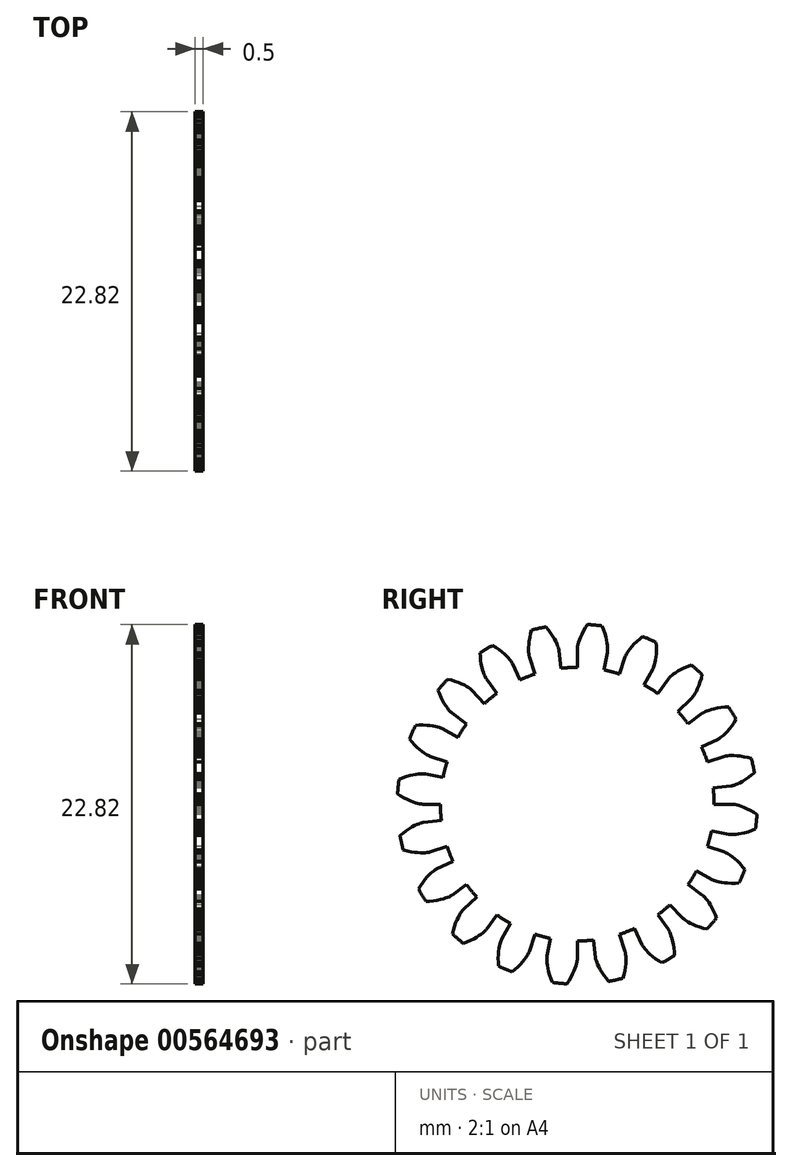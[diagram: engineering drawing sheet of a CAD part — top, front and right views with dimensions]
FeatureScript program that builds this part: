
annotation { "Feature Type Name" : "Feature", "Feature Type Description" : "" }
export const myFeature = defineFeature(function(context is Context, id is Id, definition is map)
    precondition{}
    {
        {
            assignVariable(context, id + "F0", {"name" : "GearThickness", "anyValue" : .5});
        }
        {
            var Q0;
            Q0=qCreatedBy(makeId("Right.planeOp"),FACE);
            var sketch = newSketch(context, id + "F1", { "sketchPlane" : qUnion([Q0])});
            skCircle(sketch, "E0", {"center": v(0, 0) * mm, "radius": 8.7 * mm});
            skCircle(sketch, "E1", {"center": v(0, 0) * mm, "radius": 9.84 * mm, "construction": true});
            skCircle(sketch, "E2", {"center": v(0, 0) * mm, "radius": 10.16 * mm, "construction": true});
            skCircle(sketch, "E3", {"center": v(0, 0) * mm, "radius": 11.43 * mm});
            skLineSegment(sketch, "E4", {"start": v(0, 0) * mm, "end": v(-9.84, 0) * mm, "construction": true});
            skLineSegment(sketch, "E5.1.0", {"start": v(0, 0) * mm, "end": v(-9.82, 0.5) * mm, "construction": true});
            skLineSegment(sketch, "E5.2.0", {"start": v(0, 0) * mm, "end": v(-9.79, 0.98) * mm, "construction": true});
            skLineSegment(sketch, "E5.3.0", {"start": v(0, 0) * mm, "end": v(-9.73, 1.47) * mm, "construction": true});
            skLineSegment(sketch, "E5.4.0", {"start": v(0, 0) * mm, "end": v(-9.64, 1.95) * mm, "construction": true});
            skLineSegment(sketch, "E5.5.0", {"start": v(0, 0) * mm, "end": v(-9.53, 2.43) * mm, "construction": true});
            skLineSegment(sketch, "E5.6.0", {"start": v(0, 0) * mm, "end": v(-9.4, 2.9) * mm, "construction": true});
            skLineSegment(sketch, "E5.7.0", {"start": v(0, 0) * mm, "end": v(-9.24, 3.37) * mm, "construction": true});
            skLineSegment(sketch, "E5.8.0", {"start": v(0, 0) * mm, "end": v(-9.06, 3.83) * mm, "construction": true});
            skLineSegment(sketch, "E5.9.0", {"start": v(0, 0) * mm, "end": v(-8.86, 4.28) * mm, "construction": true});
            skLineSegment(sketch, "E5.10.0", {"start": v(0, 0) * mm, "end": v(-8.63, 4.72) * mm, "construction": true});
            skLineSegment(sketch, "E5.11.0", {"start": v(0, 0) * mm, "end": v(-8.39, 5.14) * mm, "construction": true});
            skLineSegment(sketch, "E5.12.0", {"start": v(0, 0) * mm, "end": v(-8.12, 5.55) * mm, "construction": true});
            skLineSegment(sketch, "E5.13.0", {"start": v(0, 0) * mm, "end": v(-7.83, 5.95) * mm, "construction": true});
            skLineSegment(sketch, "E5.14.0", {"start": v(0, 0) * mm, "end": v(-7.52, 6.34) * mm, "construction": true});
            skLineSegment(sketch, "E5.anchor2", {"start": v(0, 0) * mm, "end": v(-7.52, 6.34) * mm, "construction": true});
            skLineSegment(sketch, "E6", {"start": v(-9.82, 0.5) * mm, "end": v(-9.85, 0) * mm, "construction": true});
            skLineSegment(sketch, "E7", {"start": v(-9.79, 0.98) * mm, "end": v(-9.89, 0) * mm, "construction": true});
            skLineSegment(sketch, "E8", {"start": v(-9.73, 1.47) * mm, "end": v(-9.95, 0.01) * mm, "construction": true});
            skLineSegment(sketch, "E9", {"start": v(-9.53, 2.43) * mm, "end": v(-10.14, 0.05) * mm, "construction": true});
            skLineSegment(sketch, "E10", {"start": v(-9.4, 2.9) * mm, "end": v(-10.27, 0.09) * mm, "construction": true});
            skLineSegment(sketch, "E11", {"start": v(-9.24, 3.37) * mm, "end": v(-10.42, 0.14) * mm, "construction": true});
            skLineSegment(sketch, "E12", {"start": v(-9.06, 3.83) * mm, "end": v(-10.6, 0.2) * mm, "construction": true});
            skLineSegment(sketch, "E13", {"start": v(-8.86, 4.28) * mm, "end": v(-10.78, 0.3) * mm, "construction": true});
            skLineSegment(sketch, "E14", {"start": v(-8.63, 4.72) * mm, "end": v(-11, 0.4) * mm, "construction": true});
            skLineSegment(sketch, "E15", {"start": v(-8.39, 5.14) * mm, "end": v(-11.21, 0.53) * mm, "construction": true});
            skLineSegment(sketch, "E16", {"start": v(-9.64, 1.95) * mm, "end": v(-10.03, 0.03) * mm, "construction": true});
            skLineSegment(sketch, "E17", {"start": v(-8.12, 5.55) * mm, "end": v(-11.45, 0.68) * mm, "construction": true});
            skLineSegment(sketch, "E18", {"start": v(-7.83, 5.95) * mm, "end": v(-11.7, 0.86) * mm, "construction": true});
            skLineSegment(sketch, "E19", {"start": v(-7.52, 6.34) * mm, "end": v(-11.96, 1.07) * mm, "construction": true});
            skLineSegment(sketch, "E20", {"start": v(0, 0) * mm, "end": v(-9.79, 0.96) * mm, "construction": true});
            skLineSegment(sketch, "E21", {"start": v(-8.7, 0) * mm, "end": v(-9.84, 0) * mm});
            skLineSegment(sketch, "E22.MirrorCS", {"start": v(-8.52, 1.7) * mm, "end": v(-9.65, 1.92) * mm});
            skLineSegment(sketch, "E23", {"start": v(-9.84, 0) * mm, "end": v(-9.85, 0) * mm});
            skLineSegment(sketch, "E24", {"start": v(-9.85, 0) * mm, "end": v(-9.89, 0) * mm});
            skLineSegment(sketch, "E25", {"start": v(-9.89, 0) * mm, "end": v(-9.95, 0.01) * mm});
            skLineSegment(sketch, "E26", {"start": v(-9.95, 0.01) * mm, "end": v(-10.03, 0.03) * mm});
            skLineSegment(sketch, "E27", {"start": v(-10.03, 0.03) * mm, "end": v(-10.14, 0.05) * mm});
            skLineSegment(sketch, "E28", {"start": v(-10.14, 0.05) * mm, "end": v(-10.27, 0.09) * mm});
            skLineSegment(sketch, "E29", {"start": v(-10.27, 0.09) * mm, "end": v(-10.42, 0.14) * mm});
            skLineSegment(sketch, "E30", {"start": v(-10.42, 0.14) * mm, "end": v(-10.6, 0.2) * mm});
            skLineSegment(sketch, "E31", {"start": v(-10.6, 0.2) * mm, "end": v(-10.78, 0.3) * mm});
            skLineSegment(sketch, "E32", {"start": v(-10.78, 0.3) * mm, "end": v(-11, 0.4) * mm});
            skLineSegment(sketch, "E33", {"start": v(-11, 0.4) * mm, "end": v(-11.21, 0.53) * mm});
            skLineSegment(sketch, "E34", {"start": v(-11.21, 0.53) * mm, "end": v(-11.45, 0.68) * mm});
            skLineSegment(sketch, "E35", {"start": v(-11.45, 0.68) * mm, "end": v(-11.7, 0.86) * mm});
            skLineSegment(sketch, "E36", {"start": v(-11.7, 0.86) * mm, "end": v(-11.96, 1.07) * mm});
            skLineSegment(sketch, "E37.MirrorCS", {"start": v(-9.65, 1.92) * mm, "end": v(-9.66, 1.92) * mm});
            skLineSegment(sketch, "E38.MirrorCS", {"start": v(-9.66, 1.92) * mm, "end": v(-9.7, 1.93) * mm});
            skLineSegment(sketch, "E39.MirrorCS", {"start": v(-9.7, 1.93) * mm, "end": v(-9.76, 1.93) * mm});
            skLineSegment(sketch, "E40.MirrorCS", {"start": v(-9.76, 1.93) * mm, "end": v(-9.84, 1.93) * mm});
            skLineSegment(sketch, "E41.MirrorCS", {"start": v(-9.95, 1.93) * mm, "end": v(-10.09, 1.92) * mm});
            skLineSegment(sketch, "E42.MirrorCS", {"start": v(-10.09, 1.92) * mm, "end": v(-10.25, 1.9) * mm});
            skLineSegment(sketch, "E43.MirrorCS", {"start": v(-10.25, 1.9) * mm, "end": v(-10.43, 1.86) * mm});
            skLineSegment(sketch, "E44.MirrorCS", {"start": v(-10.43, 1.86) * mm, "end": v(-10.63, 1.82) * mm});
            skLineSegment(sketch, "E45.MirrorCS", {"start": v(-10.86, 1.75) * mm, "end": v(-11.1, 1.67) * mm});
            skLineSegment(sketch, "E46.MirrorCS", {"start": v(-10.63, 1.82) * mm, "end": v(-10.86, 1.75) * mm});
            skLineSegment(sketch, "E47.MirrorCS", {"start": v(-11.1, 1.67) * mm, "end": v(-11.36, 1.56) * mm});
            skLineSegment(sketch, "E48.MirrorCS", {"start": v(-11.36, 1.56) * mm, "end": v(-11.64, 1.44) * mm});
            skLineSegment(sketch, "E49.MirrorCS", {"start": v(-11.64, 1.44) * mm, "end": v(-11.94, 1.28) * mm});
            skLineSegment(sketch, "E50.MirrorCS", {"start": v(-9.84, 1.93) * mm, "end": v(-9.95, 1.93) * mm});
            skLineSegment(sketch, "E51.1.0", {"start": v(-8.27, -2.69) * mm, "end": v(-9.35, -3.04) * mm});
            skLineSegment(sketch, "E51.1.1", {"start": v(-11.07, -1.84) * mm, "end": v(-11.3, -2.02) * mm});
            skLineSegment(sketch, "E51.1.2", {"start": v(-8.63, -1.02) * mm, "end": v(-9.77, -1.16) * mm});
            skLineSegment(sketch, "E51.1.3", {"start": v(-10.87, -1.69) * mm, "end": v(-11.07, -1.84) * mm});
            skLineSegment(sketch, "E51.1.4", {"start": v(-10.58, -3.02) * mm, "end": v(-10.83, -2.96) * mm});
            skLineSegment(sketch, "E51.1.5", {"start": v(-10.83, -2.96) * mm, "end": v(-11.1, -2.89) * mm});
            skLineSegment(sketch, "E51.1.6", {"start": v(-10.67, -1.56) * mm, "end": v(-10.87, -1.69) * mm});
            skLineSegment(sketch, "E51.1.7", {"start": v(-11.52, -2.23) * mm, "end": v(-11.75, -2.47) * mm});
            skLineSegment(sketch, "E51.1.8", {"start": v(-10.5, -1.45) * mm, "end": v(-10.67, -1.56) * mm});
            skLineSegment(sketch, "E51.1.9", {"start": v(-11.4, -2.8) * mm, "end": v(-11.7, -2.68) * mm});
            skLineSegment(sketch, "E51.1.10", {"start": v(-11.3, -2.02) * mm, "end": v(-11.52, -2.23) * mm});
            skLineSegment(sketch, "E51.1.11", {"start": v(-10.35, -3.05) * mm, "end": v(-10.58, -3.02) * mm});
            skLineSegment(sketch, "E51.1.12", {"start": v(-11.1, -2.89) * mm, "end": v(-11.4, -2.8) * mm});
            skLineSegment(sketch, "E51.1.13", {"start": v(-10.06, -1.24) * mm, "end": v(-10.19, -1.3) * mm});
            skLineSegment(sketch, "E51.1.14", {"start": v(-10.19, -1.3) * mm, "end": v(-10.33, -1.36) * mm});
            skLineSegment(sketch, "E51.1.15", {"start": v(-10.33, -1.36) * mm, "end": v(-10.5, -1.45) * mm});
            skLineSegment(sketch, "E51.1.16", {"start": v(-9.95, -3.09) * mm, "end": v(-10.14, -3.08) * mm});
            skLineSegment(sketch, "E51.1.17", {"start": v(-9.8, -3.09) * mm, "end": v(-9.95, -3.09) * mm});
            skLineSegment(sketch, "E51.1.18", {"start": v(-10.14, -3.08) * mm, "end": v(-10.35, -3.05) * mm});
            skLineSegment(sketch, "E51.1.19", {"start": v(-9.96, -1.2) * mm, "end": v(-10.06, -1.24) * mm});
            skLineSegment(sketch, "E51.1.20", {"start": v(-9.88, -1.18) * mm, "end": v(-9.96, -1.2) * mm});
            skLineSegment(sketch, "E51.1.21", {"start": v(-9.66, -3.08) * mm, "end": v(-9.8, -3.09) * mm});
            skLineSegment(sketch, "E51.1.22", {"start": v(-9.55, -3.07) * mm, "end": v(-9.66, -3.08) * mm});
            skLineSegment(sketch, "E51.1.23", {"start": v(-9.4, -3.05) * mm, "end": v(-9.46, -3.06) * mm});
            skLineSegment(sketch, "E51.1.24", {"start": v(-9.77, -1.16) * mm, "end": v(-9.78, -1.16) * mm});
            skLineSegment(sketch, "E51.1.25", {"start": v(-9.78, -1.16) * mm, "end": v(-9.82, -1.17) * mm});
            skLineSegment(sketch, "E51.1.26", {"start": v(-9.46, -3.06) * mm, "end": v(-9.55, -3.07) * mm});
            skLineSegment(sketch, "E51.1.27", {"start": v(-9.82, -1.17) * mm, "end": v(-9.88, -1.18) * mm});
            skLineSegment(sketch, "E51.1.28", {"start": v(-9.37, -3.04) * mm, "end": v(-9.4, -3.05) * mm});
            skLineSegment(sketch, "E51.1.29", {"start": v(-9.35, -3.04) * mm, "end": v(-9.37, -3.04) * mm});
            skLineSegment(sketch, "E51.2.0", {"start": v(-7.03, -5.1) * mm, "end": v(-7.96, -5.78) * mm});
            skLineSegment(sketch, "E51.2.1", {"start": v(-9.96, -5.18) * mm, "end": v(-10.11, -5.41) * mm});
            skLineSegment(sketch, "E51.2.2", {"start": v(-7.9, -3.64) * mm, "end": v(-8.93, -4.12) * mm});
            skLineSegment(sketch, "E51.2.3", {"start": v(-9.81, -4.96) * mm, "end": v(-9.96, -5.18) * mm});
            skLineSegment(sketch, "E51.2.4", {"start": v(-9.13, -6.14) * mm, "end": v(-9.38, -6.16) * mm});
            skLineSegment(sketch, "E51.2.5", {"start": v(-9.38, -6.16) * mm, "end": v(-9.67, -6.18) * mm});
            skLineSegment(sketch, "E51.2.6", {"start": v(-9.67, -4.78) * mm, "end": v(-9.81, -4.96) * mm});
            skLineSegment(sketch, "E51.2.7", {"start": v(-10.26, -5.68) * mm, "end": v(-10.41, -5.98) * mm});
            skLineSegment(sketch, "E51.2.8", {"start": v(-9.53, -4.62) * mm, "end": v(-9.67, -4.78) * mm});
            skLineSegment(sketch, "E51.2.9", {"start": v(-9.97, -6.18) * mm, "end": v(-10.3, -6.16) * mm});
            skLineSegment(sketch, "E51.2.10", {"start": v(-10.11, -5.41) * mm, "end": v(-10.26, -5.68) * mm});
            skLineSegment(sketch, "E51.2.11", {"start": v(-8.9, -6.1) * mm, "end": v(-9.13, -6.14) * mm});
            skLineSegment(sketch, "E51.2.12", {"start": v(-9.67, -6.18) * mm, "end": v(-9.97, -6.18) * mm});
            skLineSegment(sketch, "E51.2.13", {"start": v(-9.19, -4.3) * mm, "end": v(-9.29, -4.38) * mm});
            skLineSegment(sketch, "E51.2.14", {"start": v(-9.29, -4.38) * mm, "end": v(-9.4, -4.49) * mm});
            skLineSegment(sketch, "E51.2.15", {"start": v(-9.4, -4.49) * mm, "end": v(-9.53, -4.62) * mm});
            skLineSegment(sketch, "E51.2.16", {"start": v(-8.51, -6.01) * mm, "end": v(-8.7, -6.06) * mm});
            skLineSegment(sketch, "E51.2.17", {"start": v(-8.36, -5.97) * mm, "end": v(-8.51, -6.01) * mm});
            skLineSegment(sketch, "E51.2.18", {"start": v(-8.7, -6.06) * mm, "end": v(-8.9, -6.1) * mm});
            skLineSegment(sketch, "E51.2.19", {"start": v(-9.1, -4.22) * mm, "end": v(-9.19, -4.3) * mm});
            skLineSegment(sketch, "E51.2.20", {"start": v(-9.03, -4.17) * mm, "end": v(-9.1, -4.22) * mm});
            skLineSegment(sketch, "E51.2.21", {"start": v(-8.23, -5.92) * mm, "end": v(-8.36, -5.97) * mm});
            skLineSegment(sketch, "E51.2.22", {"start": v(-8.13, -5.88) * mm, "end": v(-8.23, -5.92) * mm});
            skLineSegment(sketch, "E51.2.23", {"start": v(-8, -5.8) * mm, "end": v(-8.05, -5.84) * mm});
            skLineSegment(sketch, "E51.2.24", {"start": v(-8.93, -4.12) * mm, "end": v(-8.94, -4.12) * mm});
            skLineSegment(sketch, "E51.2.25", {"start": v(-8.94, -4.12) * mm, "end": v(-8.98, -4.14) * mm});
            skLineSegment(sketch, "E51.2.26", {"start": v(-8.05, -5.84) * mm, "end": v(-8.13, -5.88) * mm});
            skLineSegment(sketch, "E51.2.27", {"start": v(-8.98, -4.14) * mm, "end": v(-9.03, -4.17) * mm});
            skLineSegment(sketch, "E51.2.28", {"start": v(-7.97, -5.79) * mm, "end": v(-8, -5.8) * mm});
            skLineSegment(sketch, "E51.2.29", {"start": v(-7.96, -5.78) * mm, "end": v(-7.97, -5.79) * mm});
            skLineSegment(sketch, "E51.3.0", {"start": v(-5.1, -7.03) * mm, "end": v(-5.78, -7.96) * mm});
            skLineSegment(sketch, "E51.3.1", {"start": v(-7.88, -8) * mm, "end": v(-7.94, -8.27) * mm});
            skLineSegment(sketch, "E51.3.2", {"start": v(-6.38, -5.9) * mm, "end": v(-7.22, -6.68) * mm});
            skLineSegment(sketch, "E51.3.3", {"start": v(-7.8, -7.75) * mm, "end": v(-7.88, -8) * mm});
            skLineSegment(sketch, "E51.3.4", {"start": v(-6.78, -8.66) * mm, "end": v(-7.02, -8.76) * mm});
            skLineSegment(sketch, "E51.3.5", {"start": v(-7.02, -8.76) * mm, "end": v(-7.28, -8.86) * mm});
            skLineSegment(sketch, "E51.3.6", {"start": v(-7.72, -7.53) * mm, "end": v(-7.8, -7.75) * mm});
            skLineSegment(sketch, "E51.3.7", {"start": v(-8, -8.58) * mm, "end": v(-8.06, -8.9) * mm});
            skLineSegment(sketch, "E51.3.8", {"start": v(-7.64, -7.34) * mm, "end": v(-7.72, -7.53) * mm});
            skLineSegment(sketch, "E51.3.9", {"start": v(-7.58, -8.96) * mm, "end": v(-7.9, -9.05) * mm});
            skLineSegment(sketch, "E51.3.10", {"start": v(-7.94, -8.27) * mm, "end": v(-8, -8.58) * mm});
            skLineSegment(sketch, "E51.3.11", {"start": v(-6.57, -8.55) * mm, "end": v(-6.78, -8.66) * mm});
            skLineSegment(sketch, "E51.3.12", {"start": v(-7.28, -8.86) * mm, "end": v(-7.58, -8.96) * mm});
            skLineSegment(sketch, "E51.3.13", {"start": v(-7.41, -6.92) * mm, "end": v(-7.48, -7.04) * mm});
            skLineSegment(sketch, "E51.3.14", {"start": v(-7.48, -7.04) * mm, "end": v(-7.56, -7.18) * mm});
            skLineSegment(sketch, "E51.3.15", {"start": v(-7.56, -7.18) * mm, "end": v(-7.64, -7.34) * mm});
            skLineSegment(sketch, "E51.3.16", {"start": v(-6.24, -8.35) * mm, "end": v(-6.4, -8.45) * mm});
            skLineSegment(sketch, "E51.3.17", {"start": v(-6.1, -8.26) * mm, "end": v(-6.24, -8.35) * mm});
            skLineSegment(sketch, "E51.3.18", {"start": v(-6.4, -8.45) * mm, "end": v(-6.57, -8.55) * mm});
            skLineSegment(sketch, "E51.3.19", {"start": v(-7.35, -6.83) * mm, "end": v(-7.41, -6.92) * mm});
            skLineSegment(sketch, "E51.3.20", {"start": v(-7.3, -6.76) * mm, "end": v(-7.35, -6.83) * mm});
            skLineSegment(sketch, "E51.3.21", {"start": v(-6, -8.17) * mm, "end": v(-6.1, -8.26) * mm});
            skLineSegment(sketch, "E51.3.22", {"start": v(-5.92, -8.1) * mm, "end": v(-6, -8.17) * mm});
            skLineSegment(sketch, "E51.3.23", {"start": v(-5.81, -8) * mm, "end": v(-5.86, -8.04) * mm});
            skLineSegment(sketch, "E51.3.24", {"start": v(-7.22, -6.68) * mm, "end": v(-7.23, -6.69) * mm});
            skLineSegment(sketch, "E51.3.25", {"start": v(-7.23, -6.69) * mm, "end": v(-7.26, -6.71) * mm});
            skLineSegment(sketch, "E51.3.26", {"start": v(-5.86, -8.04) * mm, "end": v(-5.92, -8.1) * mm});
            skLineSegment(sketch, "E51.3.27", {"start": v(-7.26, -6.71) * mm, "end": v(-7.3, -6.76) * mm});
            skLineSegment(sketch, "E51.3.28", {"start": v(-5.79, -7.97) * mm, "end": v(-5.81, -8) * mm});
            skLineSegment(sketch, "E51.3.29", {"start": v(-5.78, -7.96) * mm, "end": v(-5.79, -7.97) * mm});
            skLineSegment(sketch, "E51.4.0", {"start": v(-2.69, -8.27) * mm, "end": v(-3.04, -9.35) * mm});
            skLineSegment(sketch, "E51.4.1", {"start": v(-5.02, -10.04) * mm, "end": v(-5, -10.32) * mm});
            skLineSegment(sketch, "E51.4.2", {"start": v(-4.25, -7.58) * mm, "end": v(-4.8, -8.58) * mm});
            skLineSegment(sketch, "E51.4.3", {"start": v(-5.02, -9.78) * mm, "end": v(-5.02, -10.04) * mm});
            skLineSegment(sketch, "E51.4.4", {"start": v(-3.78, -10.33) * mm, "end": v(-3.97, -10.5) * mm});
            skLineSegment(sketch, "E51.4.5", {"start": v(-3.97, -10.5) * mm, "end": v(-4.19, -10.68) * mm});
            skLineSegment(sketch, "E51.4.6", {"start": v(-5.01, -9.55) * mm, "end": v(-5.02, -9.78) * mm});
            skLineSegment(sketch, "E51.4.7", {"start": v(-4.96, -10.63) * mm, "end": v(-4.9, -10.96) * mm});
            skLineSegment(sketch, "E51.4.8", {"start": v(-5, -9.34) * mm, "end": v(-5.01, -9.55) * mm});
            skLineSegment(sketch, "E51.4.9", {"start": v(-4.44, -10.86) * mm, "end": v(-4.71, -11.04) * mm});
            skLineSegment(sketch, "E51.4.10", {"start": v(-5, -10.32) * mm, "end": v(-4.96, -10.63) * mm});
            skLineSegment(sketch, "E51.4.11", {"start": v(-3.61, -10.16) * mm, "end": v(-3.78, -10.33) * mm});
            skLineSegment(sketch, "E51.4.12", {"start": v(-4.19, -10.68) * mm, "end": v(-4.44, -10.86) * mm});
            skLineSegment(sketch, "E51.4.13", {"start": v(-4.9, -8.87) * mm, "end": v(-4.94, -9) * mm});
            skLineSegment(sketch, "E51.4.14", {"start": v(-4.94, -9) * mm, "end": v(-4.97, -9.16) * mm});
            skLineSegment(sketch, "E51.4.15", {"start": v(-4.97, -9.16) * mm, "end": v(-5, -9.34) * mm});
            skLineSegment(sketch, "E51.4.16", {"start": v(-3.35, -9.87) * mm, "end": v(-3.47, -10) * mm});
            skLineSegment(sketch, "E51.4.17", {"start": v(-3.26, -9.74) * mm, "end": v(-3.35, -9.87) * mm});
            skLineSegment(sketch, "E51.4.18", {"start": v(-3.47, -10) * mm, "end": v(-3.61, -10.16) * mm});
            skLineSegment(sketch, "E51.4.19", {"start": v(-4.88, -8.76) * mm, "end": v(-4.9, -8.87) * mm});
            skLineSegment(sketch, "E51.4.20", {"start": v(-4.85, -8.68) * mm, "end": v(-4.88, -8.76) * mm});
            skLineSegment(sketch, "E51.4.21", {"start": v(-3.18, -9.63) * mm, "end": v(-3.26, -9.74) * mm});
            skLineSegment(sketch, "E51.4.22", {"start": v(-3.12, -9.53) * mm, "end": v(-3.18, -9.63) * mm});
            skLineSegment(sketch, "E51.4.23", {"start": v(-3.06, -9.4) * mm, "end": v(-3.08, -9.46) * mm});
            skLineSegment(sketch, "E51.4.24", {"start": v(-4.8, -8.58) * mm, "end": v(-4.81, -8.6) * mm});
            skLineSegment(sketch, "E51.4.25", {"start": v(-4.81, -8.6) * mm, "end": v(-4.83, -8.63) * mm});
            skLineSegment(sketch, "E51.4.26", {"start": v(-3.08, -9.46) * mm, "end": v(-3.12, -9.53) * mm});
            skLineSegment(sketch, "E51.4.27", {"start": v(-4.83, -8.63) * mm, "end": v(-4.85, -8.68) * mm});
            skLineSegment(sketch, "E51.4.28", {"start": v(-3.04, -9.37) * mm, "end": v(-3.06, -9.4) * mm});
            skLineSegment(sketch, "E51.4.29", {"start": v(-3.04, -9.35) * mm, "end": v(-3.04, -9.37) * mm});
            skLineSegment(sketch, "E51.5.0", {"start": v(0, -8.7) * mm, "end": v(0, -9.84) * mm});
            skLineSegment(sketch, "E51.5.1", {"start": v(-1.67, -11.1) * mm, "end": v(-1.56, -11.36) * mm});
            skLineSegment(sketch, "E51.5.2", {"start": v(-1.7, -8.52) * mm, "end": v(-1.92, -9.65) * mm});
            skLineSegment(sketch, "E51.5.3", {"start": v(-1.75, -10.86) * mm, "end": v(-1.67, -11.1) * mm});
            skLineSegment(sketch, "E51.5.4", {"start": v(-0.4, -11) * mm, "end": v(-0.53, -11.21) * mm});
            skLineSegment(sketch, "E51.5.5", {"start": v(-0.53, -11.21) * mm, "end": v(-0.68, -11.45) * mm});
            skLineSegment(sketch, "E51.5.6", {"start": v(-1.82, -10.63) * mm, "end": v(-1.75, -10.86) * mm});
            skLineSegment(sketch, "E51.5.7", {"start": v(-1.44, -11.64) * mm, "end": v(-1.28, -11.94) * mm});
            skLineSegment(sketch, "E51.5.8", {"start": v(-1.86, -10.43) * mm, "end": v(-1.82, -10.63) * mm});
            skLineSegment(sketch, "E51.5.9", {"start": v(-0.86, -11.7) * mm, "end": v(-1.07, -11.96) * mm});
            skLineSegment(sketch, "E51.5.10", {"start": v(-1.56, -11.36) * mm, "end": v(-1.44, -11.64) * mm});
            skLineSegment(sketch, "E51.5.11", {"start": v(-0.3, -10.78) * mm, "end": v(-0.4, -11) * mm});
            skLineSegment(sketch, "E51.5.12", {"start": v(-0.68, -11.45) * mm, "end": v(-0.86, -11.7) * mm});
            skLineSegment(sketch, "E51.5.13", {"start": v(-1.93, -9.95) * mm, "end": v(-1.92, -10.09) * mm});
            skLineSegment(sketch, "E51.5.14", {"start": v(-1.92, -10.09) * mm, "end": v(-1.9, -10.25) * mm});
            skLineSegment(sketch, "E51.5.15", {"start": v(-1.9, -10.25) * mm, "end": v(-1.86, -10.43) * mm});
            skLineSegment(sketch, "E51.5.16", {"start": v(-0.14, -10.42) * mm, "end": v(-0.2, -10.6) * mm});
            skLineSegment(sketch, "E51.5.17", {"start": v(-0.09, -10.27) * mm, "end": v(-0.14, -10.42) * mm});
            skLineSegment(sketch, "E51.5.18", {"start": v(-0.2, -10.6) * mm, "end": v(-0.3, -10.78) * mm});
            skLineSegment(sketch, "E51.5.19", {"start": v(-1.93, -9.84) * mm, "end": v(-1.93, -9.95) * mm});
            skLineSegment(sketch, "E51.5.20", {"start": v(-1.93, -9.76) * mm, "end": v(-1.93, -9.84) * mm});
            skLineSegment(sketch, "E51.5.21", {"start": v(-0.05, -10.14) * mm, "end": v(-0.09, -10.27) * mm});
            skLineSegment(sketch, "E51.5.22", {"start": v(-0.03, -10.03) * mm, "end": v(-0.05, -10.14) * mm});
            skLineSegment(sketch, "E51.5.23", {"start": v(0, -9.89) * mm, "end": v(-0.01, -9.95) * mm});
            skLineSegment(sketch, "E51.5.24", {"start": v(-1.92, -9.65) * mm, "end": v(-1.92, -9.66) * mm});
            skLineSegment(sketch, "E51.5.25", {"start": v(-1.92, -9.66) * mm, "end": v(-1.93, -9.7) * mm});
            skLineSegment(sketch, "E51.5.26", {"start": v(-0.01, -9.95) * mm, "end": v(-0.03, -10.03) * mm});
            skLineSegment(sketch, "E51.5.27", {"start": v(-1.93, -9.7) * mm, "end": v(-1.93, -9.76) * mm});
            skLineSegment(sketch, "E51.5.28", {"start": v(0, -9.85) * mm, "end": v(0, -9.89) * mm});
            skLineSegment(sketch, "E51.5.29", {"start": v(0, -9.84) * mm, "end": v(0, -9.85) * mm});
            skLineSegment(sketch, "E51.6.0", {"start": v(2.69, -8.27) * mm, "end": v(3.04, -9.35) * mm});
            skLineSegment(sketch, "E51.6.1", {"start": v(1.84, -11.07) * mm, "end": v(2.02, -11.3) * mm});
            skLineSegment(sketch, "E51.6.2", {"start": v(1.02, -8.63) * mm, "end": v(1.16, -9.77) * mm});
            skLineSegment(sketch, "E51.6.3", {"start": v(1.69, -10.87) * mm, "end": v(1.84, -11.07) * mm});
            skLineSegment(sketch, "E51.6.4", {"start": v(3.02, -10.58) * mm, "end": v(2.96, -10.83) * mm});
            skLineSegment(sketch, "E51.6.5", {"start": v(2.96, -10.83) * mm, "end": v(2.89, -11.1) * mm});
            skLineSegment(sketch, "E51.6.6", {"start": v(1.56, -10.67) * mm, "end": v(1.69, -10.87) * mm});
            skLineSegment(sketch, "E51.6.7", {"start": v(2.23, -11.52) * mm, "end": v(2.47, -11.75) * mm});
            skLineSegment(sketch, "E51.6.8", {"start": v(1.45, -10.5) * mm, "end": v(1.56, -10.67) * mm});
            skLineSegment(sketch, "E51.6.9", {"start": v(2.8, -11.4) * mm, "end": v(2.68, -11.7) * mm});
            skLineSegment(sketch, "E51.6.10", {"start": v(2.02, -11.3) * mm, "end": v(2.23, -11.52) * mm});
            skLineSegment(sketch, "E51.6.11", {"start": v(3.05, -10.35) * mm, "end": v(3.02, -10.58) * mm});
            skLineSegment(sketch, "E51.6.12", {"start": v(2.89, -11.1) * mm, "end": v(2.8, -11.4) * mm});
            skLineSegment(sketch, "E51.6.13", {"start": v(1.24, -10.06) * mm, "end": v(1.3, -10.19) * mm});
            skLineSegment(sketch, "E51.6.14", {"start": v(1.3, -10.19) * mm, "end": v(1.36, -10.33) * mm});
            skLineSegment(sketch, "E51.6.15", {"start": v(1.36, -10.33) * mm, "end": v(1.45, -10.5) * mm});
            skLineSegment(sketch, "E51.6.16", {"start": v(3.09, -9.95) * mm, "end": v(3.08, -10.14) * mm});
            skLineSegment(sketch, "E51.6.17", {"start": v(3.09, -9.8) * mm, "end": v(3.09, -9.95) * mm});
            skLineSegment(sketch, "E51.6.18", {"start": v(3.08, -10.14) * mm, "end": v(3.05, -10.35) * mm});
            skLineSegment(sketch, "E51.6.19", {"start": v(1.2, -9.96) * mm, "end": v(1.24, -10.06) * mm});
            skLineSegment(sketch, "E51.6.20", {"start": v(1.18, -9.88) * mm, "end": v(1.2, -9.96) * mm});
            skLineSegment(sketch, "E51.6.21", {"start": v(3.08, -9.66) * mm, "end": v(3.09, -9.8) * mm});
            skLineSegment(sketch, "E51.6.22", {"start": v(3.07, -9.55) * mm, "end": v(3.08, -9.66) * mm});
            skLineSegment(sketch, "E51.6.23", {"start": v(3.05, -9.4) * mm, "end": v(3.06, -9.46) * mm});
            skLineSegment(sketch, "E51.6.24", {"start": v(1.16, -9.77) * mm, "end": v(1.16, -9.78) * mm});
            skLineSegment(sketch, "E51.6.25", {"start": v(1.16, -9.78) * mm, "end": v(1.17, -9.82) * mm});
            skLineSegment(sketch, "E51.6.26", {"start": v(3.06, -9.46) * mm, "end": v(3.07, -9.55) * mm});
            skLineSegment(sketch, "E51.6.27", {"start": v(1.17, -9.82) * mm, "end": v(1.18, -9.88) * mm});
            skLineSegment(sketch, "E51.6.28", {"start": v(3.04, -9.37) * mm, "end": v(3.05, -9.4) * mm});
            skLineSegment(sketch, "E51.6.29", {"start": v(3.04, -9.35) * mm, "end": v(3.04, -9.37) * mm});
            skLineSegment(sketch, "E51.7.0", {"start": v(5.1, -7.03) * mm, "end": v(5.78, -7.96) * mm});
            skLineSegment(sketch, "E51.7.1", {"start": v(5.18, -9.96) * mm, "end": v(5.41, -10.11) * mm});
            skLineSegment(sketch, "E51.7.2", {"start": v(3.64, -7.9) * mm, "end": v(4.12, -8.93) * mm});
            skLineSegment(sketch, "E51.7.3", {"start": v(4.96, -9.81) * mm, "end": v(5.18, -9.96) * mm});
            skLineSegment(sketch, "E51.7.4", {"start": v(6.14, -9.13) * mm, "end": v(6.16, -9.38) * mm});
            skLineSegment(sketch, "E51.7.5", {"start": v(6.16, -9.38) * mm, "end": v(6.18, -9.67) * mm});
            skLineSegment(sketch, "E51.7.6", {"start": v(4.78, -9.67) * mm, "end": v(4.96, -9.81) * mm});
            skLineSegment(sketch, "E51.7.7", {"start": v(5.68, -10.26) * mm, "end": v(5.98, -10.41) * mm});
            skLineSegment(sketch, "E51.7.8", {"start": v(4.62, -9.53) * mm, "end": v(4.78, -9.67) * mm});
            skLineSegment(sketch, "E51.7.9", {"start": v(6.18, -9.97) * mm, "end": v(6.16, -10.3) * mm});
            skLineSegment(sketch, "E51.7.10", {"start": v(5.41, -10.11) * mm, "end": v(5.68, -10.26) * mm});
            skLineSegment(sketch, "E51.7.11", {"start": v(6.1, -8.9) * mm, "end": v(6.14, -9.13) * mm});
            skLineSegment(sketch, "E51.7.12", {"start": v(6.18, -9.67) * mm, "end": v(6.18, -9.97) * mm});
            skLineSegment(sketch, "E51.7.13", {"start": v(4.3, -9.19) * mm, "end": v(4.38, -9.29) * mm});
            skLineSegment(sketch, "E51.7.14", {"start": v(4.38, -9.29) * mm, "end": v(4.49, -9.4) * mm});
            skLineSegment(sketch, "E51.7.15", {"start": v(4.49, -9.4) * mm, "end": v(4.62, -9.53) * mm});
            skLineSegment(sketch, "E51.7.16", {"start": v(6.01, -8.51) * mm, "end": v(6.06, -8.7) * mm});
            skLineSegment(sketch, "E51.7.17", {"start": v(5.97, -8.36) * mm, "end": v(6.01, -8.51) * mm});
            skLineSegment(sketch, "E51.7.18", {"start": v(6.06, -8.7) * mm, "end": v(6.1, -8.9) * mm});
            skLineSegment(sketch, "E51.7.19", {"start": v(4.22, -9.1) * mm, "end": v(4.3, -9.19) * mm});
            skLineSegment(sketch, "E51.7.20", {"start": v(4.17, -9.03) * mm, "end": v(4.22, -9.1) * mm});
            skLineSegment(sketch, "E51.7.21", {"start": v(5.92, -8.23) * mm, "end": v(5.97, -8.36) * mm});
            skLineSegment(sketch, "E51.7.22", {"start": v(5.88, -8.13) * mm, "end": v(5.92, -8.23) * mm});
            skLineSegment(sketch, "E51.7.23", {"start": v(5.8, -8) * mm, "end": v(5.84, -8.05) * mm});
            skLineSegment(sketch, "E51.7.24", {"start": v(4.12, -8.93) * mm, "end": v(4.12, -8.94) * mm});
            skLineSegment(sketch, "E51.7.25", {"start": v(4.12, -8.94) * mm, "end": v(4.14, -8.98) * mm});
            skLineSegment(sketch, "E51.7.26", {"start": v(5.84, -8.05) * mm, "end": v(5.88, -8.13) * mm});
            skLineSegment(sketch, "E51.7.27", {"start": v(4.14, -8.98) * mm, "end": v(4.17, -9.03) * mm});
            skLineSegment(sketch, "E51.7.28", {"start": v(5.79, -7.97) * mm, "end": v(5.8, -8) * mm});
            skLineSegment(sketch, "E51.7.29", {"start": v(5.78, -7.96) * mm, "end": v(5.79, -7.97) * mm});
            skLineSegment(sketch, "E51.8.0", {"start": v(7.03, -5.1) * mm, "end": v(7.96, -5.78) * mm});
            skLineSegment(sketch, "E51.8.1", {"start": v(8, -7.88) * mm, "end": v(8.27, -7.94) * mm});
            skLineSegment(sketch, "E51.8.2", {"start": v(5.9, -6.38) * mm, "end": v(6.68, -7.22) * mm});
            skLineSegment(sketch, "E51.8.3", {"start": v(7.75, -7.8) * mm, "end": v(8, -7.88) * mm});
            skLineSegment(sketch, "E51.8.4", {"start": v(8.66, -6.78) * mm, "end": v(8.76, -7.02) * mm});
            skLineSegment(sketch, "E51.8.5", {"start": v(8.76, -7.02) * mm, "end": v(8.86, -7.28) * mm});
            skLineSegment(sketch, "E51.8.6", {"start": v(7.53, -7.72) * mm, "end": v(7.75, -7.8) * mm});
            skLineSegment(sketch, "E51.8.7", {"start": v(8.58, -8) * mm, "end": v(8.9, -8.06) * mm});
            skLineSegment(sketch, "E51.8.8", {"start": v(7.34, -7.64) * mm, "end": v(7.53, -7.72) * mm});
            skLineSegment(sketch, "E51.8.9", {"start": v(8.96, -7.58) * mm, "end": v(9.05, -7.9) * mm});
            skLineSegment(sketch, "E51.8.10", {"start": v(8.27, -7.94) * mm, "end": v(8.58, -8) * mm});
            skLineSegment(sketch, "E51.8.11", {"start": v(8.55, -6.57) * mm, "end": v(8.66, -6.78) * mm});
            skLineSegment(sketch, "E51.8.12", {"start": v(8.86, -7.28) * mm, "end": v(8.96, -7.58) * mm});
            skLineSegment(sketch, "E51.8.13", {"start": v(6.92, -7.41) * mm, "end": v(7.04, -7.48) * mm});
            skLineSegment(sketch, "E51.8.14", {"start": v(7.04, -7.48) * mm, "end": v(7.18, -7.56) * mm});
            skLineSegment(sketch, "E51.8.15", {"start": v(7.18, -7.56) * mm, "end": v(7.34, -7.64) * mm});
            skLineSegment(sketch, "E51.8.16", {"start": v(8.35, -6.24) * mm, "end": v(8.45, -6.4) * mm});
            skLineSegment(sketch, "E51.8.17", {"start": v(8.26, -6.1) * mm, "end": v(8.35, -6.24) * mm});
            skLineSegment(sketch, "E51.8.18", {"start": v(8.45, -6.4) * mm, "end": v(8.55, -6.57) * mm});
            skLineSegment(sketch, "E51.8.19", {"start": v(6.83, -7.35) * mm, "end": v(6.92, -7.41) * mm});
            skLineSegment(sketch, "E51.8.20", {"start": v(6.76, -7.3) * mm, "end": v(6.83, -7.35) * mm});
            skLineSegment(sketch, "E51.8.21", {"start": v(8.17, -6) * mm, "end": v(8.26, -6.1) * mm});
            skLineSegment(sketch, "E51.8.22", {"start": v(8.1, -5.92) * mm, "end": v(8.17, -6) * mm});
            skLineSegment(sketch, "E51.8.23", {"start": v(8, -5.81) * mm, "end": v(8.04, -5.86) * mm});
            skLineSegment(sketch, "E51.8.24", {"start": v(6.68, -7.22) * mm, "end": v(6.69, -7.23) * mm});
            skLineSegment(sketch, "E51.8.25", {"start": v(6.69, -7.23) * mm, "end": v(6.71, -7.26) * mm});
            skLineSegment(sketch, "E51.8.26", {"start": v(8.04, -5.86) * mm, "end": v(8.1, -5.92) * mm});
            skLineSegment(sketch, "E51.8.27", {"start": v(6.71, -7.26) * mm, "end": v(6.76, -7.3) * mm});
            skLineSegment(sketch, "E51.8.28", {"start": v(7.97, -5.79) * mm, "end": v(8, -5.81) * mm});
            skLineSegment(sketch, "E51.8.29", {"start": v(7.96, -5.78) * mm, "end": v(7.97, -5.79) * mm});
            skLineSegment(sketch, "E51.9.0", {"start": v(8.27, -2.69) * mm, "end": v(9.35, -3.04) * mm});
            skLineSegment(sketch, "E51.9.1", {"start": v(10.04, -5.02) * mm, "end": v(10.32, -5) * mm});
            skLineSegment(sketch, "E51.9.2", {"start": v(7.58, -4.25) * mm, "end": v(8.58, -4.8) * mm});
            skLineSegment(sketch, "E51.9.3", {"start": v(9.78, -5.02) * mm, "end": v(10.04, -5.02) * mm});
            skLineSegment(sketch, "E51.9.4", {"start": v(10.33, -3.78) * mm, "end": v(10.5, -3.97) * mm});
            skLineSegment(sketch, "E51.9.5", {"start": v(10.5, -3.97) * mm, "end": v(10.68, -4.19) * mm});
            skLineSegment(sketch, "E51.9.6", {"start": v(9.55, -5.01) * mm, "end": v(9.78, -5.02) * mm});
            skLineSegment(sketch, "E51.9.7", {"start": v(10.63, -4.96) * mm, "end": v(10.96, -4.9) * mm});
            skLineSegment(sketch, "E51.9.8", {"start": v(9.34, -5) * mm, "end": v(9.55, -5.01) * mm});
            skLineSegment(sketch, "E51.9.9", {"start": v(10.86, -4.44) * mm, "end": v(11.04, -4.71) * mm});
            skLineSegment(sketch, "E51.9.10", {"start": v(10.32, -5) * mm, "end": v(10.63, -4.96) * mm});
            skLineSegment(sketch, "E51.9.11", {"start": v(10.16, -3.61) * mm, "end": v(10.33, -3.78) * mm});
            skLineSegment(sketch, "E51.9.12", {"start": v(10.68, -4.19) * mm, "end": v(10.86, -4.44) * mm});
            skLineSegment(sketch, "E51.9.13", {"start": v(8.87, -4.9) * mm, "end": v(9, -4.94) * mm});
            skLineSegment(sketch, "E51.9.14", {"start": v(9, -4.94) * mm, "end": v(9.16, -4.97) * mm});
            skLineSegment(sketch, "E51.9.15", {"start": v(9.16, -4.97) * mm, "end": v(9.34, -5) * mm});
            skLineSegment(sketch, "E51.9.16", {"start": v(9.87, -3.35) * mm, "end": v(10, -3.47) * mm});
            skLineSegment(sketch, "E51.9.17", {"start": v(9.74, -3.26) * mm, "end": v(9.87, -3.35) * mm});
            skLineSegment(sketch, "E51.9.18", {"start": v(10, -3.47) * mm, "end": v(10.16, -3.61) * mm});
            skLineSegment(sketch, "E51.9.19", {"start": v(8.76, -4.88) * mm, "end": v(8.87, -4.9) * mm});
            skLineSegment(sketch, "E51.9.20", {"start": v(8.68, -4.85) * mm, "end": v(8.76, -4.88) * mm});
            skLineSegment(sketch, "E51.9.21", {"start": v(9.63, -3.18) * mm, "end": v(9.74, -3.26) * mm});
            skLineSegment(sketch, "E51.9.22", {"start": v(9.53, -3.12) * mm, "end": v(9.63, -3.18) * mm});
            skLineSegment(sketch, "E51.9.23", {"start": v(9.4, -3.06) * mm, "end": v(9.46, -3.08) * mm});
            skLineSegment(sketch, "E51.9.24", {"start": v(8.58, -4.8) * mm, "end": v(8.6, -4.81) * mm});
            skLineSegment(sketch, "E51.9.25", {"start": v(8.6, -4.81) * mm, "end": v(8.63, -4.83) * mm});
            skLineSegment(sketch, "E51.9.26", {"start": v(9.46, -3.08) * mm, "end": v(9.53, -3.12) * mm});
            skLineSegment(sketch, "E51.9.27", {"start": v(8.63, -4.83) * mm, "end": v(8.68, -4.85) * mm});
            skLineSegment(sketch, "E51.9.28", {"start": v(9.37, -3.04) * mm, "end": v(9.4, -3.06) * mm});
            skLineSegment(sketch, "E51.9.29", {"start": v(9.35, -3.04) * mm, "end": v(9.37, -3.04) * mm});
            skLineSegment(sketch, "E51.10.0", {"start": v(8.7, 0) * mm, "end": v(9.84, 0) * mm});
            skLineSegment(sketch, "E51.10.1", {"start": v(11.1, -1.67) * mm, "end": v(11.36, -1.56) * mm});
            skLineSegment(sketch, "E51.10.2", {"start": v(8.52, -1.7) * mm, "end": v(9.65, -1.92) * mm});
            skLineSegment(sketch, "E51.10.3", {"start": v(10.86, -1.75) * mm, "end": v(11.1, -1.67) * mm});
            skLineSegment(sketch, "E51.10.4", {"start": v(11, -0.4) * mm, "end": v(11.21, -0.53) * mm});
            skLineSegment(sketch, "E51.10.5", {"start": v(11.21, -0.53) * mm, "end": v(11.45, -0.68) * mm});
            skLineSegment(sketch, "E51.10.6", {"start": v(10.63, -1.82) * mm, "end": v(10.86, -1.75) * mm});
            skLineSegment(sketch, "E51.10.7", {"start": v(11.64, -1.44) * mm, "end": v(11.94, -1.28) * mm});
            skLineSegment(sketch, "E51.10.8", {"start": v(10.43, -1.86) * mm, "end": v(10.63, -1.82) * mm});
            skLineSegment(sketch, "E51.10.9", {"start": v(11.7, -0.86) * mm, "end": v(11.96, -1.07) * mm});
            skLineSegment(sketch, "E51.10.10", {"start": v(11.36, -1.56) * mm, "end": v(11.64, -1.44) * mm});
            skLineSegment(sketch, "E51.10.11", {"start": v(10.78, -0.3) * mm, "end": v(11, -0.4) * mm});
            skLineSegment(sketch, "E51.10.12", {"start": v(11.45, -0.68) * mm, "end": v(11.7, -0.86) * mm});
            skLineSegment(sketch, "E51.10.13", {"start": v(9.95, -1.93) * mm, "end": v(10.09, -1.92) * mm});
            skLineSegment(sketch, "E51.10.14", {"start": v(10.09, -1.92) * mm, "end": v(10.25, -1.9) * mm});
            skLineSegment(sketch, "E51.10.15", {"start": v(10.25, -1.9) * mm, "end": v(10.43, -1.86) * mm});
            skLineSegment(sketch, "E51.10.16", {"start": v(10.42, -0.14) * mm, "end": v(10.6, -0.2) * mm});
            skLineSegment(sketch, "E51.10.17", {"start": v(10.27, -0.09) * mm, "end": v(10.42, -0.14) * mm});
            skLineSegment(sketch, "E51.10.18", {"start": v(10.6, -0.2) * mm, "end": v(10.78, -0.3) * mm});
            skLineSegment(sketch, "E51.10.19", {"start": v(9.84, -1.93) * mm, "end": v(9.95, -1.93) * mm});
            skLineSegment(sketch, "E51.10.20", {"start": v(9.76, -1.93) * mm, "end": v(9.84, -1.93) * mm});
            skLineSegment(sketch, "E51.10.21", {"start": v(10.14, -0.05) * mm, "end": v(10.27, -0.09) * mm});
            skLineSegment(sketch, "E51.10.22", {"start": v(10.03, -0.03) * mm, "end": v(10.14, -0.05) * mm});
            skLineSegment(sketch, "E51.10.23", {"start": v(9.89, 0) * mm, "end": v(9.95, -0.01) * mm});
            skLineSegment(sketch, "E51.10.24", {"start": v(9.65, -1.92) * mm, "end": v(9.66, -1.92) * mm});
            skLineSegment(sketch, "E51.10.25", {"start": v(9.66, -1.92) * mm, "end": v(9.7, -1.93) * mm});
            skLineSegment(sketch, "E51.10.26", {"start": v(9.95, -0.01) * mm, "end": v(10.03, -0.03) * mm});
            skLineSegment(sketch, "E51.10.27", {"start": v(9.7, -1.93) * mm, "end": v(9.76, -1.93) * mm});
            skLineSegment(sketch, "E51.10.28", {"start": v(9.85, 0) * mm, "end": v(9.89, 0) * mm});
            skLineSegment(sketch, "E51.10.29", {"start": v(9.84, 0) * mm, "end": v(9.85, 0) * mm});
            skLineSegment(sketch, "E51.11.0", {"start": v(8.27, 2.69) * mm, "end": v(9.35, 3.04) * mm});
            skLineSegment(sketch, "E51.11.1", {"start": v(11.07, 1.84) * mm, "end": v(11.3, 2.02) * mm});
            skLineSegment(sketch, "E51.11.2", {"start": v(8.63, 1.02) * mm, "end": v(9.77, 1.16) * mm});
            skLineSegment(sketch, "E51.11.3", {"start": v(10.87, 1.69) * mm, "end": v(11.07, 1.84) * mm});
            skLineSegment(sketch, "E51.11.4", {"start": v(10.58, 3.02) * mm, "end": v(10.83, 2.96) * mm});
            skLineSegment(sketch, "E51.11.5", {"start": v(10.83, 2.96) * mm, "end": v(11.1, 2.89) * mm});
            skLineSegment(sketch, "E51.11.6", {"start": v(10.67, 1.56) * mm, "end": v(10.87, 1.69) * mm});
            skLineSegment(sketch, "E51.11.7", {"start": v(11.52, 2.23) * mm, "end": v(11.75, 2.47) * mm});
            skLineSegment(sketch, "E51.11.8", {"start": v(10.5, 1.45) * mm, "end": v(10.67, 1.56) * mm});
            skLineSegment(sketch, "E51.11.9", {"start": v(11.4, 2.8) * mm, "end": v(11.7, 2.68) * mm});
            skLineSegment(sketch, "E51.11.10", {"start": v(11.3, 2.02) * mm, "end": v(11.52, 2.23) * mm});
            skLineSegment(sketch, "E51.11.11", {"start": v(10.35, 3.05) * mm, "end": v(10.58, 3.02) * mm});
            skLineSegment(sketch, "E51.11.12", {"start": v(11.1, 2.89) * mm, "end": v(11.4, 2.8) * mm});
            skLineSegment(sketch, "E51.11.13", {"start": v(10.06, 1.24) * mm, "end": v(10.19, 1.3) * mm});
            skLineSegment(sketch, "E51.11.14", {"start": v(10.19, 1.3) * mm, "end": v(10.33, 1.36) * mm});
            skLineSegment(sketch, "E51.11.15", {"start": v(10.33, 1.36) * mm, "end": v(10.5, 1.45) * mm});
            skLineSegment(sketch, "E51.11.16", {"start": v(9.95, 3.09) * mm, "end": v(10.14, 3.08) * mm});
            skLineSegment(sketch, "E51.11.17", {"start": v(9.8, 3.09) * mm, "end": v(9.95, 3.09) * mm});
            skLineSegment(sketch, "E51.11.18", {"start": v(10.14, 3.08) * mm, "end": v(10.35, 3.05) * mm});
            skLineSegment(sketch, "E51.11.19", {"start": v(9.96, 1.2) * mm, "end": v(10.06, 1.24) * mm});
            skLineSegment(sketch, "E51.11.20", {"start": v(9.88, 1.18) * mm, "end": v(9.96, 1.2) * mm});
            skLineSegment(sketch, "E51.11.21", {"start": v(9.66, 3.08) * mm, "end": v(9.8, 3.09) * mm});
            skLineSegment(sketch, "E51.11.22", {"start": v(9.55, 3.07) * mm, "end": v(9.66, 3.08) * mm});
            skLineSegment(sketch, "E51.11.23", {"start": v(9.4, 3.05) * mm, "end": v(9.46, 3.06) * mm});
            skLineSegment(sketch, "E51.11.24", {"start": v(9.77, 1.16) * mm, "end": v(9.78, 1.16) * mm});
            skLineSegment(sketch, "E51.11.25", {"start": v(9.78, 1.16) * mm, "end": v(9.82, 1.17) * mm});
            skLineSegment(sketch, "E51.11.26", {"start": v(9.46, 3.06) * mm, "end": v(9.55, 3.07) * mm});
            skLineSegment(sketch, "E51.11.27", {"start": v(9.82, 1.17) * mm, "end": v(9.88, 1.18) * mm});
            skLineSegment(sketch, "E51.11.28", {"start": v(9.37, 3.04) * mm, "end": v(9.4, 3.05) * mm});
            skLineSegment(sketch, "E51.11.29", {"start": v(9.35, 3.04) * mm, "end": v(9.37, 3.04) * mm});
            skLineSegment(sketch, "E51.12.0", {"start": v(7.03, 5.1) * mm, "end": v(7.96, 5.78) * mm});
            skLineSegment(sketch, "E51.12.1", {"start": v(9.96, 5.18) * mm, "end": v(10.11, 5.41) * mm});
            skLineSegment(sketch, "E51.12.2", {"start": v(7.9, 3.64) * mm, "end": v(8.93, 4.12) * mm});
            skLineSegment(sketch, "E51.12.3", {"start": v(9.81, 4.96) * mm, "end": v(9.96, 5.18) * mm});
            skLineSegment(sketch, "E51.12.4", {"start": v(9.13, 6.14) * mm, "end": v(9.38, 6.16) * mm});
            skLineSegment(sketch, "E51.12.5", {"start": v(9.38, 6.16) * mm, "end": v(9.67, 6.18) * mm});
            skLineSegment(sketch, "E51.12.6", {"start": v(9.67, 4.78) * mm, "end": v(9.81, 4.96) * mm});
            skLineSegment(sketch, "E51.12.7", {"start": v(10.26, 5.68) * mm, "end": v(10.41, 5.98) * mm});
            skLineSegment(sketch, "E51.12.8", {"start": v(9.53, 4.62) * mm, "end": v(9.67, 4.78) * mm});
            skLineSegment(sketch, "E51.12.9", {"start": v(9.97, 6.18) * mm, "end": v(10.3, 6.16) * mm});
            skLineSegment(sketch, "E51.12.10", {"start": v(10.11, 5.41) * mm, "end": v(10.26, 5.68) * mm});
            skLineSegment(sketch, "E51.12.11", {"start": v(8.9, 6.1) * mm, "end": v(9.13, 6.14) * mm});
            skLineSegment(sketch, "E51.12.12", {"start": v(9.67, 6.18) * mm, "end": v(9.97, 6.18) * mm});
            skLineSegment(sketch, "E51.12.13", {"start": v(9.19, 4.3) * mm, "end": v(9.29, 4.38) * mm});
            skLineSegment(sketch, "E51.12.14", {"start": v(9.29, 4.38) * mm, "end": v(9.4, 4.49) * mm});
            skLineSegment(sketch, "E51.12.15", {"start": v(9.4, 4.49) * mm, "end": v(9.53, 4.62) * mm});
            skLineSegment(sketch, "E51.12.16", {"start": v(8.51, 6.01) * mm, "end": v(8.7, 6.06) * mm});
            skLineSegment(sketch, "E51.12.17", {"start": v(8.36, 5.97) * mm, "end": v(8.51, 6.01) * mm});
            skLineSegment(sketch, "E51.12.18", {"start": v(8.7, 6.06) * mm, "end": v(8.9, 6.1) * mm});
            skLineSegment(sketch, "E51.12.19", {"start": v(9.1, 4.22) * mm, "end": v(9.19, 4.3) * mm});
            skLineSegment(sketch, "E51.12.20", {"start": v(9.03, 4.17) * mm, "end": v(9.1, 4.22) * mm});
            skLineSegment(sketch, "E51.12.21", {"start": v(8.23, 5.92) * mm, "end": v(8.36, 5.97) * mm});
            skLineSegment(sketch, "E51.12.22", {"start": v(8.13, 5.88) * mm, "end": v(8.23, 5.92) * mm});
            skLineSegment(sketch, "E51.12.23", {"start": v(8, 5.8) * mm, "end": v(8.05, 5.84) * mm});
            skLineSegment(sketch, "E51.12.24", {"start": v(8.93, 4.12) * mm, "end": v(8.94, 4.12) * mm});
            skLineSegment(sketch, "E51.12.25", {"start": v(8.94, 4.12) * mm, "end": v(8.98, 4.14) * mm});
            skLineSegment(sketch, "E51.12.26", {"start": v(8.05, 5.84) * mm, "end": v(8.13, 5.88) * mm});
            skLineSegment(sketch, "E51.12.27", {"start": v(8.98, 4.14) * mm, "end": v(9.03, 4.17) * mm});
            skLineSegment(sketch, "E51.12.28", {"start": v(7.97, 5.79) * mm, "end": v(8, 5.8) * mm});
            skLineSegment(sketch, "E51.12.29", {"start": v(7.96, 5.78) * mm, "end": v(7.97, 5.79) * mm});
            skLineSegment(sketch, "E51.13.0", {"start": v(5.1, 7.03) * mm, "end": v(5.78, 7.96) * mm});
            skLineSegment(sketch, "E51.13.1", {"start": v(7.88, 8) * mm, "end": v(7.94, 8.27) * mm});
            skLineSegment(sketch, "E51.13.2", {"start": v(6.38, 5.9) * mm, "end": v(7.22, 6.68) * mm});
            skLineSegment(sketch, "E51.13.3", {"start": v(7.8, 7.75) * mm, "end": v(7.88, 8) * mm});
            skLineSegment(sketch, "E51.13.4", {"start": v(6.78, 8.66) * mm, "end": v(7.02, 8.76) * mm});
            skLineSegment(sketch, "E51.13.5", {"start": v(7.02, 8.76) * mm, "end": v(7.28, 8.86) * mm});
            skLineSegment(sketch, "E51.13.6", {"start": v(7.72, 7.53) * mm, "end": v(7.8, 7.75) * mm});
            skLineSegment(sketch, "E51.13.7", {"start": v(8, 8.58) * mm, "end": v(8.06, 8.9) * mm});
            skLineSegment(sketch, "E51.13.8", {"start": v(7.64, 7.34) * mm, "end": v(7.72, 7.53) * mm});
            skLineSegment(sketch, "E51.13.9", {"start": v(7.58, 8.96) * mm, "end": v(7.9, 9.05) * mm});
            skLineSegment(sketch, "E51.13.10", {"start": v(7.94, 8.27) * mm, "end": v(8, 8.58) * mm});
            skLineSegment(sketch, "E51.13.11", {"start": v(6.57, 8.55) * mm, "end": v(6.78, 8.66) * mm});
            skLineSegment(sketch, "E51.13.12", {"start": v(7.28, 8.86) * mm, "end": v(7.58, 8.96) * mm});
            skLineSegment(sketch, "E51.13.13", {"start": v(7.41, 6.92) * mm, "end": v(7.48, 7.04) * mm});
            skLineSegment(sketch, "E51.13.14", {"start": v(7.48, 7.04) * mm, "end": v(7.56, 7.18) * mm});
            skLineSegment(sketch, "E51.13.15", {"start": v(7.56, 7.18) * mm, "end": v(7.64, 7.34) * mm});
            skLineSegment(sketch, "E51.13.16", {"start": v(6.24, 8.35) * mm, "end": v(6.4, 8.45) * mm});
            skLineSegment(sketch, "E51.13.17", {"start": v(6.1, 8.26) * mm, "end": v(6.24, 8.35) * mm});
            skLineSegment(sketch, "E51.13.18", {"start": v(6.4, 8.45) * mm, "end": v(6.57, 8.55) * mm});
            skLineSegment(sketch, "E51.13.19", {"start": v(7.35, 6.83) * mm, "end": v(7.41, 6.92) * mm});
            skLineSegment(sketch, "E51.13.20", {"start": v(7.3, 6.76) * mm, "end": v(7.35, 6.83) * mm});
            skLineSegment(sketch, "E51.13.21", {"start": v(6, 8.17) * mm, "end": v(6.1, 8.26) * mm});
            skLineSegment(sketch, "E51.13.22", {"start": v(5.92, 8.1) * mm, "end": v(6, 8.17) * mm});
            skLineSegment(sketch, "E51.13.23", {"start": v(5.81, 8) * mm, "end": v(5.86, 8.04) * mm});
            skLineSegment(sketch, "E51.13.24", {"start": v(7.22, 6.68) * mm, "end": v(7.23, 6.69) * mm});
            skLineSegment(sketch, "E51.13.25", {"start": v(7.23, 6.69) * mm, "end": v(7.26, 6.71) * mm});
            skLineSegment(sketch, "E51.13.26", {"start": v(5.86, 8.04) * mm, "end": v(5.92, 8.1) * mm});
            skLineSegment(sketch, "E51.13.27", {"start": v(7.26, 6.71) * mm, "end": v(7.3, 6.76) * mm});
            skLineSegment(sketch, "E51.13.28", {"start": v(5.79, 7.97) * mm, "end": v(5.81, 8) * mm});
            skLineSegment(sketch, "E51.13.29", {"start": v(5.78, 7.96) * mm, "end": v(5.79, 7.97) * mm});
            skLineSegment(sketch, "E51.14.0", {"start": v(2.69, 8.27) * mm, "end": v(3.04, 9.35) * mm});
            skLineSegment(sketch, "E51.14.1", {"start": v(5.02, 10.04) * mm, "end": v(5, 10.32) * mm});
            skLineSegment(sketch, "E51.14.2", {"start": v(4.25, 7.58) * mm, "end": v(4.8, 8.58) * mm});
            skLineSegment(sketch, "E51.14.3", {"start": v(5.02, 9.78) * mm, "end": v(5.02, 10.04) * mm});
            skLineSegment(sketch, "E51.14.4", {"start": v(3.78, 10.33) * mm, "end": v(3.97, 10.5) * mm});
            skLineSegment(sketch, "E51.14.5", {"start": v(3.97, 10.5) * mm, "end": v(4.19, 10.68) * mm});
            skLineSegment(sketch, "E51.14.6", {"start": v(5.01, 9.55) * mm, "end": v(5.02, 9.78) * mm});
            skLineSegment(sketch, "E51.14.7", {"start": v(4.96, 10.63) * mm, "end": v(4.9, 10.96) * mm});
            skLineSegment(sketch, "E51.14.8", {"start": v(5, 9.34) * mm, "end": v(5.01, 9.55) * mm});
            skLineSegment(sketch, "E51.14.9", {"start": v(4.44, 10.86) * mm, "end": v(4.71, 11.04) * mm});
            skLineSegment(sketch, "E51.14.10", {"start": v(5, 10.32) * mm, "end": v(4.96, 10.63) * mm});
            skLineSegment(sketch, "E51.14.11", {"start": v(3.61, 10.16) * mm, "end": v(3.78, 10.33) * mm});
            skLineSegment(sketch, "E51.14.12", {"start": v(4.19, 10.68) * mm, "end": v(4.44, 10.86) * mm});
            skLineSegment(sketch, "E51.14.13", {"start": v(4.9, 8.87) * mm, "end": v(4.94, 9) * mm});
            skLineSegment(sketch, "E51.14.14", {"start": v(4.94, 9) * mm, "end": v(4.97, 9.16) * mm});
            skLineSegment(sketch, "E51.14.15", {"start": v(4.97, 9.16) * mm, "end": v(5, 9.34) * mm});
            skLineSegment(sketch, "E51.14.16", {"start": v(3.35, 9.87) * mm, "end": v(3.47, 10) * mm});
            skLineSegment(sketch, "E51.14.17", {"start": v(3.26, 9.74) * mm, "end": v(3.35, 9.87) * mm});
            skLineSegment(sketch, "E51.14.18", {"start": v(3.47, 10) * mm, "end": v(3.61, 10.16) * mm});
            skLineSegment(sketch, "E51.14.19", {"start": v(4.88, 8.76) * mm, "end": v(4.9, 8.87) * mm});
            skLineSegment(sketch, "E51.14.20", {"start": v(4.85, 8.68) * mm, "end": v(4.88, 8.76) * mm});
            skLineSegment(sketch, "E51.14.21", {"start": v(3.18, 9.63) * mm, "end": v(3.26, 9.74) * mm});
            skLineSegment(sketch, "E51.14.22", {"start": v(3.12, 9.53) * mm, "end": v(3.18, 9.63) * mm});
            skLineSegment(sketch, "E51.14.23", {"start": v(3.06, 9.4) * mm, "end": v(3.08, 9.46) * mm});
            skLineSegment(sketch, "E51.14.24", {"start": v(4.8, 8.58) * mm, "end": v(4.81, 8.6) * mm});
            skLineSegment(sketch, "E51.14.25", {"start": v(4.81, 8.6) * mm, "end": v(4.83, 8.63) * mm});
            skLineSegment(sketch, "E51.14.26", {"start": v(3.08, 9.46) * mm, "end": v(3.12, 9.53) * mm});
            skLineSegment(sketch, "E51.14.27", {"start": v(4.83, 8.63) * mm, "end": v(4.85, 8.68) * mm});
            skLineSegment(sketch, "E51.14.28", {"start": v(3.04, 9.37) * mm, "end": v(3.06, 9.4) * mm});
            skLineSegment(sketch, "E51.14.29", {"start": v(3.04, 9.35) * mm, "end": v(3.04, 9.37) * mm});
            skLineSegment(sketch, "E51.15.0", {"start": v(0, 8.7) * mm, "end": v(0, 9.84) * mm});
            skLineSegment(sketch, "E51.15.1", {"start": v(1.67, 11.1) * mm, "end": v(1.56, 11.36) * mm});
            skLineSegment(sketch, "E51.15.2", {"start": v(1.7, 8.52) * mm, "end": v(1.92, 9.65) * mm});
            skLineSegment(sketch, "E51.15.3", {"start": v(1.75, 10.86) * mm, "end": v(1.67, 11.1) * mm});
            skLineSegment(sketch, "E51.15.4", {"start": v(0.4, 11) * mm, "end": v(0.53, 11.21) * mm});
            skLineSegment(sketch, "E51.15.5", {"start": v(0.53, 11.21) * mm, "end": v(0.68, 11.45) * mm});
            skLineSegment(sketch, "E51.15.6", {"start": v(1.82, 10.63) * mm, "end": v(1.75, 10.86) * mm});
            skLineSegment(sketch, "E51.15.7", {"start": v(1.44, 11.64) * mm, "end": v(1.28, 11.94) * mm});
            skLineSegment(sketch, "E51.15.8", {"start": v(1.86, 10.43) * mm, "end": v(1.82, 10.63) * mm});
            skLineSegment(sketch, "E51.15.9", {"start": v(0.86, 11.7) * mm, "end": v(1.07, 11.96) * mm});
            skLineSegment(sketch, "E51.15.10", {"start": v(1.56, 11.36) * mm, "end": v(1.44, 11.64) * mm});
            skLineSegment(sketch, "E51.15.11", {"start": v(0.3, 10.78) * mm, "end": v(0.4, 11) * mm});
            skLineSegment(sketch, "E51.15.12", {"start": v(0.68, 11.45) * mm, "end": v(0.86, 11.7) * mm});
            skLineSegment(sketch, "E51.15.13", {"start": v(1.93, 9.95) * mm, "end": v(1.92, 10.09) * mm});
            skLineSegment(sketch, "E51.15.14", {"start": v(1.92, 10.09) * mm, "end": v(1.9, 10.25) * mm});
            skLineSegment(sketch, "E51.15.15", {"start": v(1.9, 10.25) * mm, "end": v(1.86, 10.43) * mm});
            skLineSegment(sketch, "E51.15.16", {"start": v(0.14, 10.42) * mm, "end": v(0.2, 10.6) * mm});
            skLineSegment(sketch, "E51.15.17", {"start": v(0.09, 10.27) * mm, "end": v(0.14, 10.42) * mm});
            skLineSegment(sketch, "E51.15.18", {"start": v(0.2, 10.6) * mm, "end": v(0.3, 10.78) * mm});
            skLineSegment(sketch, "E51.15.19", {"start": v(1.93, 9.84) * mm, "end": v(1.93, 9.95) * mm});
            skLineSegment(sketch, "E51.15.20", {"start": v(1.93, 9.76) * mm, "end": v(1.93, 9.84) * mm});
            skLineSegment(sketch, "E51.15.21", {"start": v(0.05, 10.14) * mm, "end": v(0.09, 10.27) * mm});
            skLineSegment(sketch, "E51.15.22", {"start": v(0.03, 10.03) * mm, "end": v(0.05, 10.14) * mm});
            skLineSegment(sketch, "E51.15.23", {"start": v(0, 9.89) * mm, "end": v(0.01, 9.95) * mm});
            skLineSegment(sketch, "E51.15.24", {"start": v(1.92, 9.65) * mm, "end": v(1.92, 9.66) * mm});
            skLineSegment(sketch, "E51.15.25", {"start": v(1.92, 9.66) * mm, "end": v(1.93, 9.7) * mm});
            skLineSegment(sketch, "E51.15.26", {"start": v(0.01, 9.95) * mm, "end": v(0.03, 10.03) * mm});
            skLineSegment(sketch, "E51.15.27", {"start": v(1.93, 9.7) * mm, "end": v(1.93, 9.76) * mm});
            skLineSegment(sketch, "E51.15.28", {"start": v(0, 9.85) * mm, "end": v(0, 9.89) * mm});
            skLineSegment(sketch, "E51.15.29", {"start": v(0, 9.84) * mm, "end": v(0, 9.85) * mm});
            skLineSegment(sketch, "E51.16.0", {"start": v(-2.69, 8.27) * mm, "end": v(-3.04, 9.35) * mm});
            skLineSegment(sketch, "E51.16.1", {"start": v(-1.84, 11.07) * mm, "end": v(-2.02, 11.3) * mm});
            skLineSegment(sketch, "E51.16.2", {"start": v(-1.02, 8.63) * mm, "end": v(-1.16, 9.77) * mm});
            skLineSegment(sketch, "E51.16.3", {"start": v(-1.69, 10.87) * mm, "end": v(-1.84, 11.07) * mm});
            skLineSegment(sketch, "E51.16.4", {"start": v(-3.02, 10.58) * mm, "end": v(-2.96, 10.83) * mm});
            skLineSegment(sketch, "E51.16.5", {"start": v(-2.96, 10.83) * mm, "end": v(-2.89, 11.1) * mm});
            skLineSegment(sketch, "E51.16.6", {"start": v(-1.56, 10.67) * mm, "end": v(-1.69, 10.87) * mm});
            skLineSegment(sketch, "E51.16.7", {"start": v(-2.23, 11.52) * mm, "end": v(-2.47, 11.75) * mm});
            skLineSegment(sketch, "E51.16.8", {"start": v(-1.45, 10.5) * mm, "end": v(-1.56, 10.67) * mm});
            skLineSegment(sketch, "E51.16.9", {"start": v(-2.8, 11.4) * mm, "end": v(-2.68, 11.7) * mm});
            skLineSegment(sketch, "E51.16.10", {"start": v(-2.02, 11.3) * mm, "end": v(-2.23, 11.52) * mm});
            skLineSegment(sketch, "E51.16.11", {"start": v(-3.05, 10.35) * mm, "end": v(-3.02, 10.58) * mm});
            skLineSegment(sketch, "E51.16.12", {"start": v(-2.89, 11.1) * mm, "end": v(-2.8, 11.4) * mm});
            skLineSegment(sketch, "E51.16.13", {"start": v(-1.24, 10.06) * mm, "end": v(-1.3, 10.19) * mm});
            skLineSegment(sketch, "E51.16.14", {"start": v(-1.3, 10.19) * mm, "end": v(-1.36, 10.33) * mm});
            skLineSegment(sketch, "E51.16.15", {"start": v(-1.36, 10.33) * mm, "end": v(-1.45, 10.5) * mm});
            skLineSegment(sketch, "E51.16.16", {"start": v(-3.09, 9.95) * mm, "end": v(-3.08, 10.14) * mm});
            skLineSegment(sketch, "E51.16.17", {"start": v(-3.09, 9.8) * mm, "end": v(-3.09, 9.95) * mm});
            skLineSegment(sketch, "E51.16.18", {"start": v(-3.08, 10.14) * mm, "end": v(-3.05, 10.35) * mm});
            skLineSegment(sketch, "E51.16.19", {"start": v(-1.2, 9.96) * mm, "end": v(-1.24, 10.06) * mm});
            skLineSegment(sketch, "E51.16.20", {"start": v(-1.18, 9.88) * mm, "end": v(-1.2, 9.96) * mm});
            skLineSegment(sketch, "E51.16.21", {"start": v(-3.08, 9.66) * mm, "end": v(-3.09, 9.8) * mm});
            skLineSegment(sketch, "E51.16.22", {"start": v(-3.07, 9.55) * mm, "end": v(-3.08, 9.66) * mm});
            skLineSegment(sketch, "E51.16.23", {"start": v(-3.05, 9.4) * mm, "end": v(-3.06, 9.46) * mm});
            skLineSegment(sketch, "E51.16.24", {"start": v(-1.16, 9.77) * mm, "end": v(-1.16, 9.78) * mm});
            skLineSegment(sketch, "E51.16.25", {"start": v(-1.16, 9.78) * mm, "end": v(-1.17, 9.82) * mm});
            skLineSegment(sketch, "E51.16.26", {"start": v(-3.06, 9.46) * mm, "end": v(-3.07, 9.55) * mm});
            skLineSegment(sketch, "E51.16.27", {"start": v(-1.17, 9.82) * mm, "end": v(-1.18, 9.88) * mm});
            skLineSegment(sketch, "E51.16.28", {"start": v(-3.04, 9.37) * mm, "end": v(-3.05, 9.4) * mm});
            skLineSegment(sketch, "E51.16.29", {"start": v(-3.04, 9.35) * mm, "end": v(-3.04, 9.37) * mm});
            skLineSegment(sketch, "E51.17.0", {"start": v(-5.1, 7.03) * mm, "end": v(-5.78, 7.96) * mm});
            skLineSegment(sketch, "E51.17.1", {"start": v(-5.18, 9.96) * mm, "end": v(-5.41, 10.11) * mm});
            skLineSegment(sketch, "E51.17.2", {"start": v(-3.64, 7.9) * mm, "end": v(-4.12, 8.93) * mm});
            skLineSegment(sketch, "E51.17.3", {"start": v(-4.96, 9.81) * mm, "end": v(-5.18, 9.96) * mm});
            skLineSegment(sketch, "E51.17.4", {"start": v(-6.14, 9.13) * mm, "end": v(-6.16, 9.38) * mm});
            skLineSegment(sketch, "E51.17.5", {"start": v(-6.16, 9.38) * mm, "end": v(-6.18, 9.67) * mm});
            skLineSegment(sketch, "E51.17.6", {"start": v(-4.78, 9.67) * mm, "end": v(-4.96, 9.81) * mm});
            skLineSegment(sketch, "E51.17.7", {"start": v(-5.68, 10.26) * mm, "end": v(-5.98, 10.41) * mm});
            skLineSegment(sketch, "E51.17.8", {"start": v(-4.62, 9.53) * mm, "end": v(-4.78, 9.67) * mm});
            skLineSegment(sketch, "E51.17.9", {"start": v(-6.18, 9.97) * mm, "end": v(-6.16, 10.3) * mm});
            skLineSegment(sketch, "E51.17.10", {"start": v(-5.41, 10.11) * mm, "end": v(-5.68, 10.26) * mm});
            skLineSegment(sketch, "E51.17.11", {"start": v(-6.1, 8.9) * mm, "end": v(-6.14, 9.13) * mm});
            skLineSegment(sketch, "E51.17.12", {"start": v(-6.18, 9.67) * mm, "end": v(-6.18, 9.97) * mm});
            skLineSegment(sketch, "E51.17.13", {"start": v(-4.3, 9.19) * mm, "end": v(-4.38, 9.29) * mm});
            skLineSegment(sketch, "E51.17.14", {"start": v(-4.38, 9.29) * mm, "end": v(-4.49, 9.4) * mm});
            skLineSegment(sketch, "E51.17.15", {"start": v(-4.49, 9.4) * mm, "end": v(-4.62, 9.53) * mm});
            skLineSegment(sketch, "E51.17.16", {"start": v(-6.01, 8.51) * mm, "end": v(-6.06, 8.7) * mm});
            skLineSegment(sketch, "E51.17.17", {"start": v(-5.97, 8.36) * mm, "end": v(-6.01, 8.51) * mm});
            skLineSegment(sketch, "E51.17.18", {"start": v(-6.06, 8.7) * mm, "end": v(-6.1, 8.9) * mm});
            skLineSegment(sketch, "E51.17.19", {"start": v(-4.22, 9.1) * mm, "end": v(-4.3, 9.19) * mm});
            skLineSegment(sketch, "E51.17.20", {"start": v(-4.17, 9.03) * mm, "end": v(-4.22, 9.1) * mm});
            skLineSegment(sketch, "E51.17.21", {"start": v(-5.92, 8.23) * mm, "end": v(-5.97, 8.36) * mm});
            skLineSegment(sketch, "E51.17.22", {"start": v(-5.88, 8.13) * mm, "end": v(-5.92, 8.23) * mm});
            skLineSegment(sketch, "E51.17.23", {"start": v(-5.8, 8) * mm, "end": v(-5.84, 8.05) * mm});
            skLineSegment(sketch, "E51.17.24", {"start": v(-4.12, 8.93) * mm, "end": v(-4.12, 8.94) * mm});
            skLineSegment(sketch, "E51.17.25", {"start": v(-4.12, 8.94) * mm, "end": v(-4.14, 8.98) * mm});
            skLineSegment(sketch, "E51.17.26", {"start": v(-5.84, 8.05) * mm, "end": v(-5.88, 8.13) * mm});
            skLineSegment(sketch, "E51.17.27", {"start": v(-4.14, 8.98) * mm, "end": v(-4.17, 9.03) * mm});
            skLineSegment(sketch, "E51.17.28", {"start": v(-5.79, 7.97) * mm, "end": v(-5.8, 8) * mm});
            skLineSegment(sketch, "E51.17.29", {"start": v(-5.78, 7.96) * mm, "end": v(-5.79, 7.97) * mm});
            skLineSegment(sketch, "E51.18.0", {"start": v(-7.03, 5.1) * mm, "end": v(-7.96, 5.78) * mm});
            skLineSegment(sketch, "E51.18.1", {"start": v(-8, 7.88) * mm, "end": v(-8.27, 7.94) * mm});
            skLineSegment(sketch, "E51.18.2", {"start": v(-5.9, 6.38) * mm, "end": v(-6.68, 7.22) * mm});
            skLineSegment(sketch, "E51.18.3", {"start": v(-7.75, 7.8) * mm, "end": v(-8, 7.88) * mm});
            skLineSegment(sketch, "E51.18.4", {"start": v(-8.66, 6.78) * mm, "end": v(-8.76, 7.02) * mm});
            skLineSegment(sketch, "E51.18.5", {"start": v(-8.76, 7.02) * mm, "end": v(-8.86, 7.28) * mm});
            skLineSegment(sketch, "E51.18.6", {"start": v(-7.53, 7.72) * mm, "end": v(-7.75, 7.8) * mm});
            skLineSegment(sketch, "E51.18.7", {"start": v(-8.58, 8) * mm, "end": v(-8.9, 8.06) * mm});
            skLineSegment(sketch, "E51.18.8", {"start": v(-7.34, 7.64) * mm, "end": v(-7.53, 7.72) * mm});
            skLineSegment(sketch, "E51.18.9", {"start": v(-8.96, 7.58) * mm, "end": v(-9.05, 7.9) * mm});
            skLineSegment(sketch, "E51.18.10", {"start": v(-8.27, 7.94) * mm, "end": v(-8.58, 8) * mm});
            skLineSegment(sketch, "E51.18.11", {"start": v(-8.55, 6.57) * mm, "end": v(-8.66, 6.78) * mm});
            skLineSegment(sketch, "E51.18.12", {"start": v(-8.86, 7.28) * mm, "end": v(-8.96, 7.58) * mm});
            skLineSegment(sketch, "E51.18.13", {"start": v(-6.92, 7.41) * mm, "end": v(-7.04, 7.48) * mm});
            skLineSegment(sketch, "E51.18.14", {"start": v(-7.04, 7.48) * mm, "end": v(-7.18, 7.56) * mm});
            skLineSegment(sketch, "E51.18.15", {"start": v(-7.18, 7.56) * mm, "end": v(-7.34, 7.64) * mm});
            skLineSegment(sketch, "E51.18.16", {"start": v(-8.35, 6.24) * mm, "end": v(-8.45, 6.4) * mm});
            skLineSegment(sketch, "E51.18.17", {"start": v(-8.26, 6.1) * mm, "end": v(-8.35, 6.24) * mm});
            skLineSegment(sketch, "E51.18.18", {"start": v(-8.45, 6.4) * mm, "end": v(-8.55, 6.57) * mm});
            skLineSegment(sketch, "E51.18.19", {"start": v(-6.83, 7.35) * mm, "end": v(-6.92, 7.41) * mm});
            skLineSegment(sketch, "E51.18.20", {"start": v(-6.76, 7.3) * mm, "end": v(-6.83, 7.35) * mm});
            skLineSegment(sketch, "E51.18.21", {"start": v(-8.17, 6) * mm, "end": v(-8.26, 6.1) * mm});
            skLineSegment(sketch, "E51.18.22", {"start": v(-8.1, 5.92) * mm, "end": v(-8.17, 6) * mm});
            skLineSegment(sketch, "E51.18.23", {"start": v(-8, 5.81) * mm, "end": v(-8.04, 5.86) * mm});
            skLineSegment(sketch, "E51.18.24", {"start": v(-6.68, 7.22) * mm, "end": v(-6.69, 7.23) * mm});
            skLineSegment(sketch, "E51.18.25", {"start": v(-6.69, 7.23) * mm, "end": v(-6.71, 7.26) * mm});
            skLineSegment(sketch, "E51.18.26", {"start": v(-8.04, 5.86) * mm, "end": v(-8.1, 5.92) * mm});
            skLineSegment(sketch, "E51.18.27", {"start": v(-6.71, 7.26) * mm, "end": v(-6.76, 7.3) * mm});
            skLineSegment(sketch, "E51.18.28", {"start": v(-7.97, 5.79) * mm, "end": v(-8, 5.81) * mm});
            skLineSegment(sketch, "E51.18.29", {"start": v(-7.96, 5.78) * mm, "end": v(-7.97, 5.79) * mm});
            skLineSegment(sketch, "E51.19.0", {"start": v(-8.27, 2.69) * mm, "end": v(-9.35, 3.04) * mm});
            skLineSegment(sketch, "E51.19.1", {"start": v(-10.04, 5.02) * mm, "end": v(-10.32, 5) * mm});
            skLineSegment(sketch, "E51.19.2", {"start": v(-7.58, 4.25) * mm, "end": v(-8.58, 4.8) * mm});
            skLineSegment(sketch, "E51.19.3", {"start": v(-9.78, 5.02) * mm, "end": v(-10.04, 5.02) * mm});
            skLineSegment(sketch, "E51.19.4", {"start": v(-10.33, 3.78) * mm, "end": v(-10.5, 3.97) * mm});
            skLineSegment(sketch, "E51.19.5", {"start": v(-10.5, 3.97) * mm, "end": v(-10.68, 4.19) * mm});
            skLineSegment(sketch, "E51.19.6", {"start": v(-9.55, 5.01) * mm, "end": v(-9.78, 5.02) * mm});
            skLineSegment(sketch, "E51.19.7", {"start": v(-10.63, 4.96) * mm, "end": v(-10.96, 4.9) * mm});
            skLineSegment(sketch, "E51.19.8", {"start": v(-9.34, 5) * mm, "end": v(-9.55, 5.01) * mm});
            skLineSegment(sketch, "E51.19.9", {"start": v(-10.86, 4.44) * mm, "end": v(-11.04, 4.71) * mm});
            skLineSegment(sketch, "E51.19.10", {"start": v(-10.32, 5) * mm, "end": v(-10.63, 4.96) * mm});
            skLineSegment(sketch, "E51.19.11", {"start": v(-10.16, 3.61) * mm, "end": v(-10.33, 3.78) * mm});
            skLineSegment(sketch, "E51.19.12", {"start": v(-10.68, 4.19) * mm, "end": v(-10.86, 4.44) * mm});
            skLineSegment(sketch, "E51.19.13", {"start": v(-8.87, 4.9) * mm, "end": v(-9, 4.94) * mm});
            skLineSegment(sketch, "E51.19.14", {"start": v(-9, 4.94) * mm, "end": v(-9.16, 4.97) * mm});
            skLineSegment(sketch, "E51.19.15", {"start": v(-9.16, 4.97) * mm, "end": v(-9.34, 5) * mm});
            skLineSegment(sketch, "E51.19.16", {"start": v(-9.87, 3.35) * mm, "end": v(-10, 3.47) * mm});
            skLineSegment(sketch, "E51.19.17", {"start": v(-9.74, 3.26) * mm, "end": v(-9.87, 3.35) * mm});
            skLineSegment(sketch, "E51.19.18", {"start": v(-10, 3.47) * mm, "end": v(-10.16, 3.61) * mm});
            skLineSegment(sketch, "E51.19.19", {"start": v(-8.76, 4.88) * mm, "end": v(-8.87, 4.9) * mm});
            skLineSegment(sketch, "E51.19.20", {"start": v(-8.68, 4.85) * mm, "end": v(-8.76, 4.88) * mm});
            skLineSegment(sketch, "E51.19.21", {"start": v(-9.63, 3.18) * mm, "end": v(-9.74, 3.26) * mm});
            skLineSegment(sketch, "E51.19.22", {"start": v(-9.53, 3.12) * mm, "end": v(-9.63, 3.18) * mm});
            skLineSegment(sketch, "E51.19.23", {"start": v(-9.4, 3.06) * mm, "end": v(-9.46, 3.08) * mm});
            skLineSegment(sketch, "E51.19.24", {"start": v(-8.58, 4.8) * mm, "end": v(-8.6, 4.81) * mm});
            skLineSegment(sketch, "E51.19.25", {"start": v(-8.6, 4.81) * mm, "end": v(-8.63, 4.83) * mm});
            skLineSegment(sketch, "E51.19.26", {"start": v(-9.46, 3.08) * mm, "end": v(-9.53, 3.12) * mm});
            skLineSegment(sketch, "E51.19.27", {"start": v(-8.63, 4.83) * mm, "end": v(-8.68, 4.85) * mm});
            skLineSegment(sketch, "E51.19.28", {"start": v(-9.37, 3.04) * mm, "end": v(-9.4, 3.06) * mm});
            skLineSegment(sketch, "E51.19.29", {"start": v(-9.35, 3.04) * mm, "end": v(-9.37, 3.04) * mm});
            skSolve(sketch);
        }
        {
            var Q0;
            {var subQ0=sQuery(id+"F1.wireOp",EDGE,"E0");var subQ27=makeQuery(id+"F1.imprint","INTERSECT",VERTEX,{"derivedFrom":[subQ0,sQuery(id+"F1.wireOp",EDGE,"E51.10.0")]});Q0=makeQuery(id+"F1.imprint","IMPRINT",FACE,{"disambiguationData":[TD([[makeQuery(id+"F1.imprint","IMPRINT",EDGE,{"disambiguationData":[TD([[subQ27,-1.0]])],"derivedFrom":subQ0}),1.0]])]});}
            var Q1;
            {var subQ0=sQuery(id+"F1.wireOp",EDGE,"E51.1.0");Q1=makeQuery(id+"F1.imprint","IMPRINT",FACE,{"disambiguationData":[TD([[makeQuery(id+"F1.imprint","IMPRINT",EDGE,{"derivedFrom":subQ0}),-1.0]])]});}
            var Q2;
            {var subQ7=sQuery(id+"F1.wireOp",EDGE,"E51.2.0");Q2=makeQuery(id+"F1.imprint","IMPRINT",FACE,{"disambiguationData":[TD([[makeQuery(id+"F1.imprint","IMPRINT",EDGE,{"derivedFrom":subQ7}),-1.0]])]});}
            var Q3;
            {var subQ8=sQuery(id+"F1.wireOp",EDGE,"E51.3.0");Q3=makeQuery(id+"F1.imprint","IMPRINT",FACE,{"disambiguationData":[TD([[makeQuery(id+"F1.imprint","IMPRINT",EDGE,{"derivedFrom":subQ8}),-1.0]])]});}
            var Q4;
            {var subQ2=sQuery(id+"F1.wireOp",EDGE,"E51.4.0");Q4=makeQuery(id+"F1.imprint","IMPRINT",FACE,{"disambiguationData":[TD([[makeQuery(id+"F1.imprint","IMPRINT",EDGE,{"derivedFrom":subQ2}),-1.0]])]});}
            var Q5;
            {var subQ8=sQuery(id+"F1.wireOp",EDGE,"E51.5.0");Q5=makeQuery(id+"F1.imprint","IMPRINT",FACE,{"disambiguationData":[TD([[makeQuery(id+"F1.imprint","IMPRINT",EDGE,{"derivedFrom":subQ8}),-1.0]])]});}
            var Q6;
            {var subQ3=sQuery(id+"F1.wireOp",EDGE,"E51.6.0");Q6=makeQuery(id+"F1.imprint","IMPRINT",FACE,{"disambiguationData":[TD([[makeQuery(id+"F1.imprint","IMPRINT",EDGE,{"derivedFrom":subQ3}),-1.0]])]});}
            var Q7;
            {var subQ0=sQuery(id+"F1.wireOp",EDGE,"E51.7.0");Q7=makeQuery(id+"F1.imprint","IMPRINT",FACE,{"disambiguationData":[TD([[makeQuery(id+"F1.imprint","IMPRINT",EDGE,{"derivedFrom":subQ0}),-1.0]])]});}
            var Q8;
            {var subQ5=sQuery(id+"F1.wireOp",EDGE,"E51.8.0");Q8=makeQuery(id+"F1.imprint","IMPRINT",FACE,{"disambiguationData":[TD([[makeQuery(id+"F1.imprint","IMPRINT",EDGE,{"derivedFrom":subQ5}),-1.0]])]});}
            var Q9;
            {var subQ1=sQuery(id+"F1.wireOp",EDGE,"E51.9.0");Q9=makeQuery(id+"F1.imprint","IMPRINT",FACE,{"disambiguationData":[TD([[makeQuery(id+"F1.imprint","IMPRINT",EDGE,{"derivedFrom":subQ1}),-1.0]])]});}
            var Q10;
            {var subQ5=sQuery(id+"F1.wireOp",EDGE,"E51.10.0");Q10=makeQuery(id+"F1.imprint","IMPRINT",FACE,{"disambiguationData":[TD([[makeQuery(id+"F1.imprint","IMPRINT",EDGE,{"derivedFrom":subQ5}),-1.0]])]});}
            var Q11;
            {var subQ8=sQuery(id+"F1.wireOp",EDGE,"E51.11.0");Q11=makeQuery(id+"F1.imprint","IMPRINT",FACE,{"disambiguationData":[TD([[makeQuery(id+"F1.imprint","IMPRINT",EDGE,{"derivedFrom":subQ8}),-1.0]])]});}
            var Q12;
            {var subQ2=sQuery(id+"F1.wireOp",EDGE,"E51.12.0");Q12=makeQuery(id+"F1.imprint","IMPRINT",FACE,{"disambiguationData":[TD([[makeQuery(id+"F1.imprint","IMPRINT",EDGE,{"derivedFrom":subQ2}),-1.0]])]});}
            var Q13;
            {var subQ3=sQuery(id+"F1.wireOp",EDGE,"E51.13.0");Q13=makeQuery(id+"F1.imprint","IMPRINT",FACE,{"disambiguationData":[TD([[makeQuery(id+"F1.imprint","IMPRINT",EDGE,{"derivedFrom":subQ3}),-1.0]])]});}
            var Q14;
            {var subQ0=sQuery(id+"F1.wireOp",EDGE,"E51.14.0");Q14=makeQuery(id+"F1.imprint","IMPRINT",FACE,{"disambiguationData":[TD([[makeQuery(id+"F1.imprint","IMPRINT",EDGE,{"derivedFrom":subQ0}),-1.0]])]});}
            var Q15;
            {var subQ6=sQuery(id+"F1.wireOp",EDGE,"E51.15.0");Q15=makeQuery(id+"F1.imprint","IMPRINT",FACE,{"disambiguationData":[TD([[makeQuery(id+"F1.imprint","IMPRINT",EDGE,{"derivedFrom":subQ6}),-1.0]])]});}
            var Q16;
            {var subQ5=sQuery(id+"F1.wireOp",EDGE,"E51.16.0");Q16=makeQuery(id+"F1.imprint","IMPRINT",FACE,{"disambiguationData":[TD([[makeQuery(id+"F1.imprint","IMPRINT",EDGE,{"derivedFrom":subQ5}),-1.0]])]});}
            var Q17;
            {var subQ7=sQuery(id+"F1.wireOp",EDGE,"E51.17.0");Q17=makeQuery(id+"F1.imprint","IMPRINT",FACE,{"disambiguationData":[TD([[makeQuery(id+"F1.imprint","IMPRINT",EDGE,{"derivedFrom":subQ7}),-1.0]])]});}
            var Q18;
            {var subQ5=sQuery(id+"F1.wireOp",EDGE,"E51.18.0");Q18=makeQuery(id+"F1.imprint","IMPRINT",FACE,{"disambiguationData":[TD([[makeQuery(id+"F1.imprint","IMPRINT",EDGE,{"derivedFrom":subQ5}),-1.0]])]});}
            var Q19;
            {var subQ8=sQuery(id+"F1.wireOp",EDGE,"E51.19.0");Q19=makeQuery(id+"F1.imprint","IMPRINT",FACE,{"disambiguationData":[TD([[makeQuery(id+"F1.imprint","IMPRINT",EDGE,{"derivedFrom":subQ8}),-1.0]])]});}
            var Q20;
            {var subQ8=sQuery(id+"F1.wireOp",EDGE,"E21");Q20=makeQuery(id+"F1.imprint","IMPRINT",FACE,{"disambiguationData":[TD([[makeQuery(id+"F1.imprint","IMPRINT",EDGE,{"derivedFrom":subQ8}),-1.0]])]});}
            extrude(context, id + "F2", {"entities" : qUnion([Q0, Q1, Q2, Q3, Q4, Q5, Q6, Q7, Q8, Q9, Q10, Q11, Q12, Q13, Q14, Q15, Q16, Q17, Q18, Q19, Q20]), "depth" : (getVariable(context, 'GearThickness')) * mm});
        }
    });
